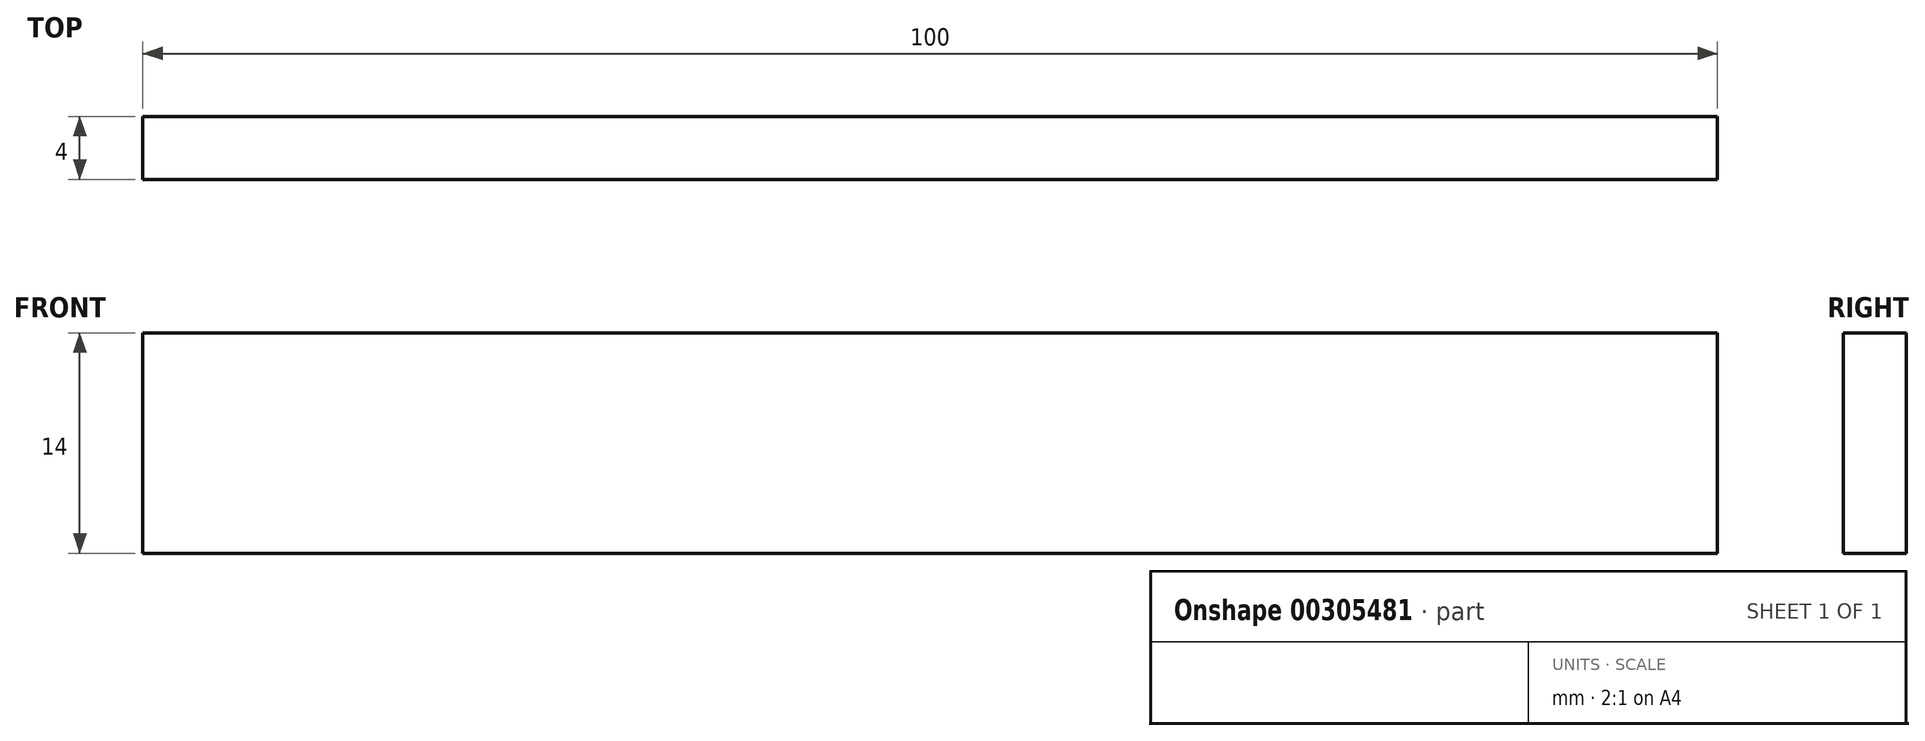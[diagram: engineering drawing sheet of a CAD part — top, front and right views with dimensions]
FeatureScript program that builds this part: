
annotation { "Feature Type Name" : "Feature", "Feature Type Description" : "" }
export const myFeature = defineFeature(function(context is Context, id is Id, definition is map)
    precondition{}
    {
        {
            var Q0;
            Q0=qCreatedBy(makeId("Top.planeOp"),FACE);
            var sketch = newSketch(context, id + "F0", { "sketchPlane" : qUnion([Q0])});
            skLineSegment(sketch, "E0.bottom", {"start": v(-50, -18.04) * mm, "end": v(50, -18.04) * mm});
            skLineSegment(sketch, "E0.top", {"start": v(-50, -14.04) * mm, "end": v(50, -14.04) * mm});
            skLineSegment(sketch, "E0.left", {"start": v(-50, -18.04) * mm, "end": v(-50, -14.04) * mm});
            skLineSegment(sketch, "E0.right", {"start": v(50, -18.04) * mm, "end": v(50, -14.04) * mm});
            skSolve(sketch);
        }
        {
            var Q0;
            Q0 = qSketchRegion(id + "F0", true);
            extrude(context, id + "F1", {"entities" : qUnion([Q0]), "depth" : 14 * mm});
        }
    });
